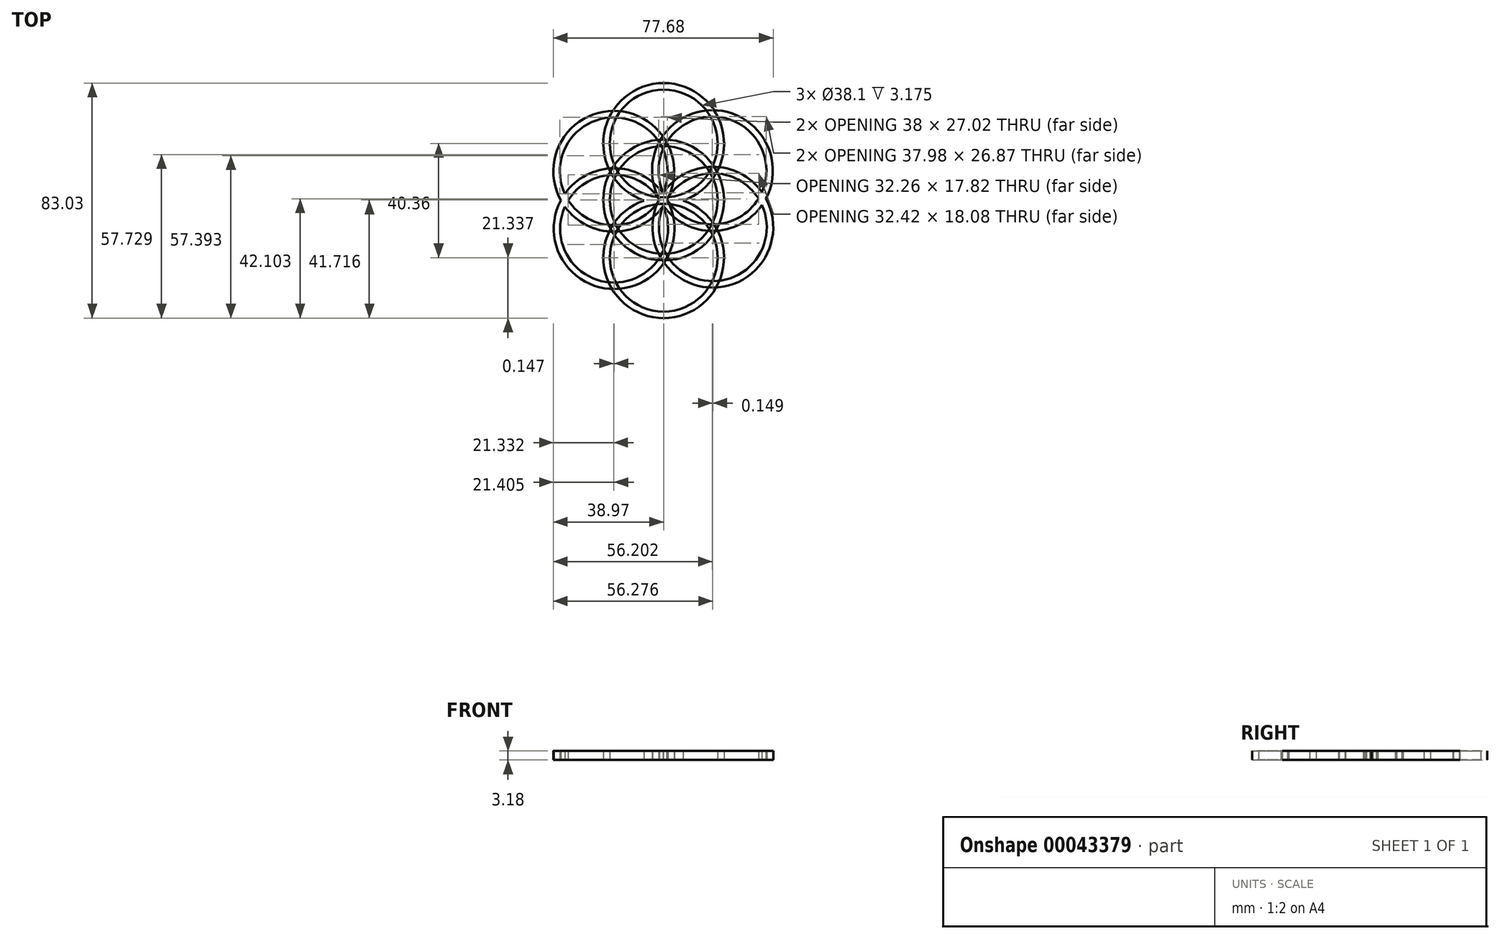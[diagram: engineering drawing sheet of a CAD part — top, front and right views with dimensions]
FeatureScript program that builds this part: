
annotation { "Feature Type Name" : "Feature", "Feature Type Description" : "" }
export const myFeature = defineFeature(function(context is Context, id is Id, definition is map)
    precondition{}
    {
        {
            var Q0;
            Q0=qCreatedBy(makeId("Top.planeOp"),FACE);
            var sketch = newSketch(context, id + "F0", { "sketchPlane" : qUnion([Q0])});
            skCircle(sketch, "E0", {"center": v(0, 0) * mm, "radius": 19.05 * mm});
            skCircle(sketch, "E1.0", {"center": v(0, 0) * mm, "radius": 21.34 * mm});
            skSolve(sketch);
        }
        {
            var Q0;
            Q0=makeQuery(id+"F0.imprint","IMPRINT",FACE,{"disambiguationData":[TD([[makeQuery(id+"F0.imprint","IMPRINT",EDGE,{"derivedFrom":sQuery(id+"F0.wireOp",EDGE,"E0")}),-1.0]])]});
            var Q1;
            Q1=sQuery(id+"F0.wireOp",EDGE,"E1.0");
            var Q2;
            Q2=sQuery(id+"F0.wireOp",EDGE,"E0");
            extrude(context, id + "F1", {"entities" : qUnion([Q0]), "surfaceEntities" : qUnion([Q1, Q2]), "depth" : 3.17 * mm});
        }
        {
            var Q0;
            Q0=qCreatedBy(makeId("Top.planeOp"),FACE);
            var sketch = newSketch(context, id + "F2", { "sketchPlane" : qUnion([Q0])});
            skCircle(sketch, "E2", {"center": v(0, 19.98) * mm, "radius": 19.05 * mm});
            skCircle(sketch, "E3.0", {"center": v(0, 19.98) * mm, "radius": 21.34 * mm});
            skCircle(sketch, "E4", {"center": v(0, -20.38) * mm, "radius": 19.05 * mm});
            skCircle(sketch, "E5.0", {"center": v(0, -20.38) * mm, "radius": 21.34 * mm});
            skSolve(sketch);
        }
        {
            var Q0;
            {var subQ0=sQuery(id+"F2.wireOp",EDGE,"E5.0");var subQ1=sQuery(id+"F2.wireOp",EDGE,"E2");var subQ2=makeQuery(id+"F2.imprint","INTERSECT",VERTEX,{"disambiguationData":[OD(0.0)],"derivedFrom":[subQ1,subQ0]});Q0=makeQuery(id+"F2.imprint","IMPRINT",FACE,{"disambiguationData":[TD([[makeQuery(id+"F2.imprint","IMPRINT",EDGE,{"disambiguationData":[TD([[subQ2,1.0]])],"derivedFrom":subQ1}),-1.0]])]});}
            var Q1;
            {var subQ1=sQuery(id+"F2.wireOp",EDGE,"E5.0");var subQ4=sQuery(id+"F2.wireOp",EDGE,"E2");var subQ6=makeQuery(id+"F2.imprint","INTERSECT",VERTEX,{"disambiguationData":[OD(0.0)],"derivedFrom":[subQ4,subQ1]});Q1=makeQuery(id+"F2.imprint","IMPRINT",FACE,{"disambiguationData":[TD([[makeQuery(id+"F2.imprint","IMPRINT",EDGE,{"disambiguationData":[TD([[subQ6,-1.0]])],"derivedFrom":subQ4}),-1.0]])]});}
            var Q2;
            {var subQ1=sQuery(id+"F2.wireOp",EDGE,"E3.0");var subQ4=sQuery(id+"F2.wireOp",EDGE,"E5.0");var subQ6=makeQuery(id+"F2.imprint","INTERSECT",VERTEX,{"disambiguationData":[OD(0.0)],"derivedFrom":[subQ1,subQ4]});Q2=makeQuery(id+"F2.imprint","IMPRINT",FACE,{"disambiguationData":[TD([[makeQuery(id+"F2.imprint","IMPRINT",EDGE,{"disambiguationData":[TD([[subQ6,-1.0]])],"derivedFrom":subQ1}),-1.0]])]});}
            extrude(context, id + "F3", {"entities" : qUnion([Q0, Q1, Q2]), "depth" : 3.17 * mm});
        }
        {
            var Q0;
            Q0=qCreatedBy(makeId("Top.planeOp"),FACE);
            var sketch = newSketch(context, id + "F4", { "sketchPlane" : qUnion([Q0])});
            skCircle(sketch, "E6", {"center": v(-17.63, 10.13) * mm, "radius": 19.05 * mm});
            skCircle(sketch, "E7.0", {"center": v(-17.63, 10.13) * mm, "radius": 21.34 * mm});
            skCircle(sketch, "E8", {"center": v(-17.5, -10.14) * mm, "radius": 19.05 * mm});
            skCircle(sketch, "E9.0", {"center": v(-17.5, -10.14) * mm, "radius": 21.34 * mm});
            skSolve(sketch);
        }
        {
            var Q0;
            Q0 = qSketchRegion(id + "F4", true);
            var Q1;
            {var subQ1=sQuery(id+"F4.wireOp",EDGE,"E6");var subQ4=sQuery(id+"F4.wireOp",EDGE,"E8");var subQ6=makeQuery(id+"F4.imprint","INTERSECT",VERTEX,{"disambiguationData":[OD(0.0)],"derivedFrom":[subQ1,subQ4]});Q1=makeQuery(id+"F4.imprint","IMPRINT",FACE,{"disambiguationData":[TD([[makeQuery(id+"F4.imprint","IMPRINT",EDGE,{"disambiguationData":[TD([[subQ6,1.0]])],"derivedFrom":subQ1}),1.0]])]});}
            var Q2;
            {var subQ0=sQuery(id+"F4.wireOp",EDGE,"E8");var subQ3=sQuery(id+"F4.wireOp",EDGE,"E6");var subQ4=makeQuery(id+"F4.imprint","INTERSECT",VERTEX,{"disambiguationData":[OD(0.0)],"derivedFrom":[subQ3,subQ0]});Q2=makeQuery(id+"F4.imprint","IMPRINT",FACE,{"disambiguationData":[TD([[makeQuery(id+"F4.imprint","IMPRINT",EDGE,{"disambiguationData":[TD([[subQ4,-1.0]])],"derivedFrom":subQ3}),-1.0]])]});}
            extrude(context, id + "F5", {"entities" : qUnion([Q0, Q1, Q2]), "depth" : 3.17 * mm});
        }
        {
            var Q0;
            Q0=qCreatedBy(makeId("Top.planeOp"),FACE);
            var sketch = newSketch(context, id + "F6", { "sketchPlane" : qUnion([Q0])});
            skCircle(sketch, "E10", {"center": v(17.24, 10.4) * mm, "radius": 19.05 * mm});
            skCircle(sketch, "E11.0", {"center": v(17.24, 10.4) * mm, "radius": 21.34 * mm});
            skCircle(sketch, "E12", {"center": v(17.37, -9.63) * mm, "radius": 19.05 * mm});
            skCircle(sketch, "E13.0", {"center": v(17.37, -9.63) * mm, "radius": 21.34 * mm});
            skSolve(sketch);
        }
        {
            var Q0;
            Q0 = qSketchRegion(id + "F6", true);
            var Q1;
            {var subQ1=sQuery(id+"F6.wireOp",EDGE,"E10");var subQ4=sQuery(id+"F6.wireOp",EDGE,"E12");var subQ6=makeQuery(id+"F6.imprint","INTERSECT",VERTEX,{"disambiguationData":[OD(0.0)],"derivedFrom":[subQ1,subQ4]});Q1=makeQuery(id+"F6.imprint","IMPRINT",FACE,{"disambiguationData":[TD([[makeQuery(id+"F6.imprint","IMPRINT",EDGE,{"disambiguationData":[TD([[subQ6,1.0]])],"derivedFrom":subQ1}),1.0]])]});}
            var Q2;
            {var subQ0=sQuery(id+"F6.wireOp",EDGE,"E12");var subQ3=sQuery(id+"F6.wireOp",EDGE,"E10");var subQ4=makeQuery(id+"F6.imprint","INTERSECT",VERTEX,{"disambiguationData":[OD(0.0)],"derivedFrom":[subQ3,subQ0]});Q2=makeQuery(id+"F6.imprint","IMPRINT",FACE,{"disambiguationData":[TD([[makeQuery(id+"F6.imprint","IMPRINT",EDGE,{"disambiguationData":[TD([[subQ4,-1.0]])],"derivedFrom":subQ3}),-1.0]])]});}
            extrude(context, id + "F7", {"entities" : qUnion([Q0, Q1, Q2]), "depth" : 3.17 * mm});
        }
    });
